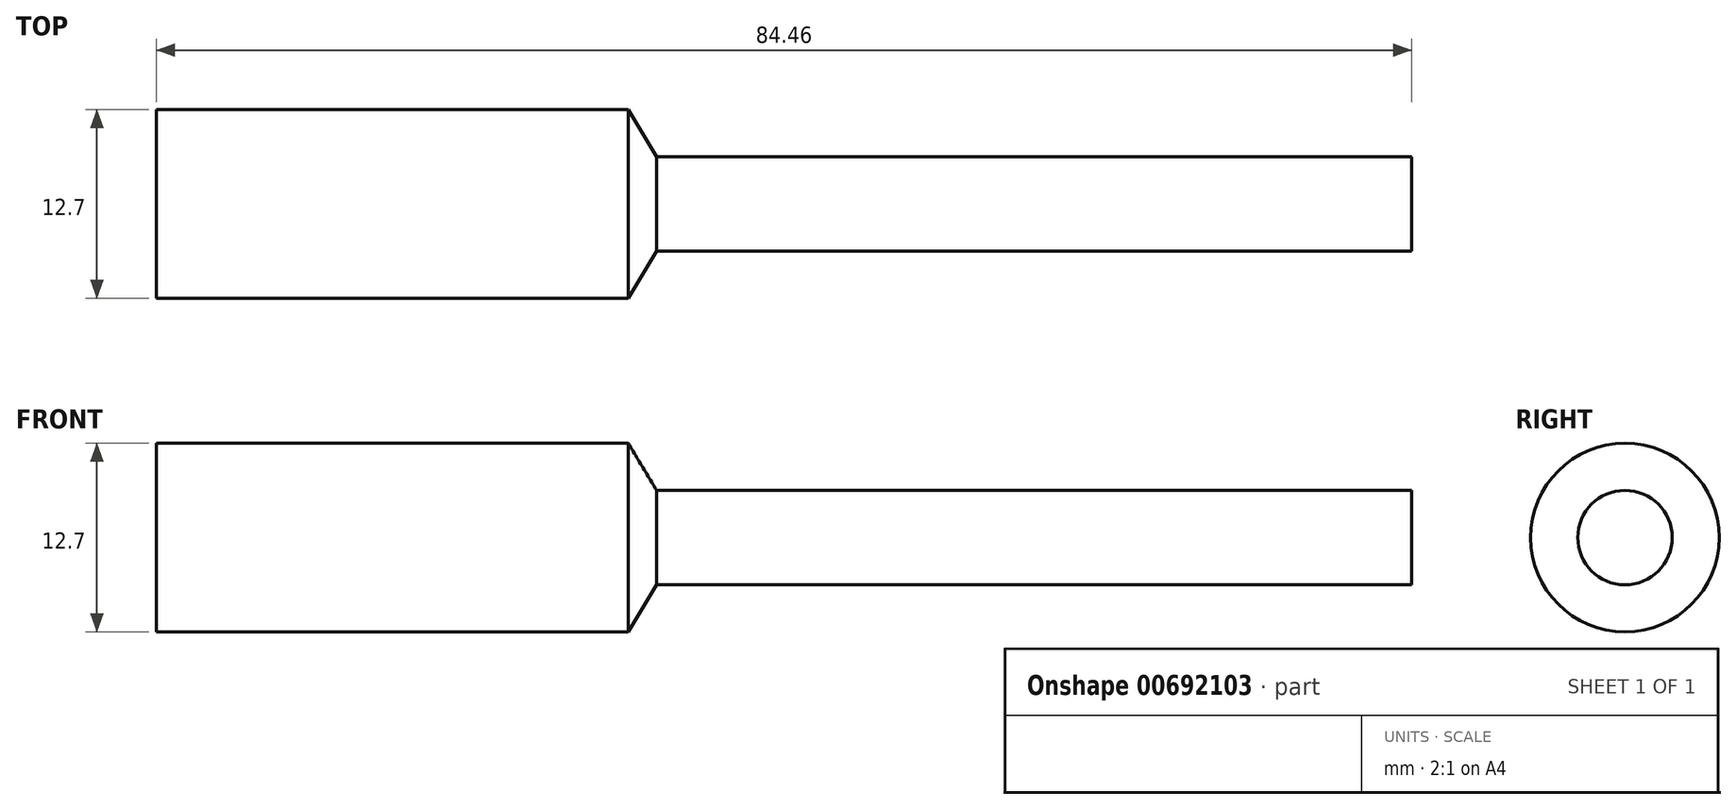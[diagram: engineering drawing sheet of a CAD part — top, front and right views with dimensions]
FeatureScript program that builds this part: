
annotation { "Feature Type Name" : "Feature", "Feature Type Description" : "" }
export const myFeature = defineFeature(function(context is Context, id is Id, definition is map)
    precondition{}
    {
        {
            var Q0;
            Q0=qCreatedBy(makeId("Front.planeOp"),FACE);
            var sketch = newSketch(context, id + "F0", { "sketchPlane" : qUnion([Q0])});
            skLineSegment(sketch, "E0", {"start": v(0, 6.35) * mm, "end": v(31.75, 6.35) * mm});
            skLineSegment(sketch, "E1", {"start": v(31.75, 6.35) * mm, "end": v(33.66, 3.17) * mm});
            skLineSegment(sketch, "E2", {"start": v(33.66, 3.17) * mm, "end": v(84.46, 3.17) * mm});
            skLineSegment(sketch, "E3", {"start": v(84.46, 3.17) * mm, "end": v(84.46, 0) * mm});
            skLineSegment(sketch, "E4", {"start": v(-4.04, 0) * mm, "end": v(41.77, 0) * mm, "construction": true});
            skLineSegment(sketch, "E5", {"start": v(0, 6.35) * mm, "end": v(0, 0) * mm});
            skLineSegment(sketch, "E6", {"start": v(0, 0) * mm, "end": v(84.46, 0) * mm});
            skSolve(sketch);
        }
        {
            var Q0;
            Q0=makeQuery(id+"F0.imprint","IMPRINT",FACE,{"disambiguationData":[TD([[makeQuery(id+"F0.imprint","IMPRINT",EDGE,{"derivedFrom":sQuery(id+"F0.wireOp",EDGE,"E0")}),-1.0]])]});
            var Q1;
            Q1=sQuery(id+"F0.wireOp",EDGE,"E6");
            revolve(context, id + "F1", {"surfaceOperationType" : NewSurfaceOperationType.NEW, "entities" : qUnion([Q0]), "axis" : qUnion([Q1]), "revolveType" : RevolveType.FULL});
        }
    });
